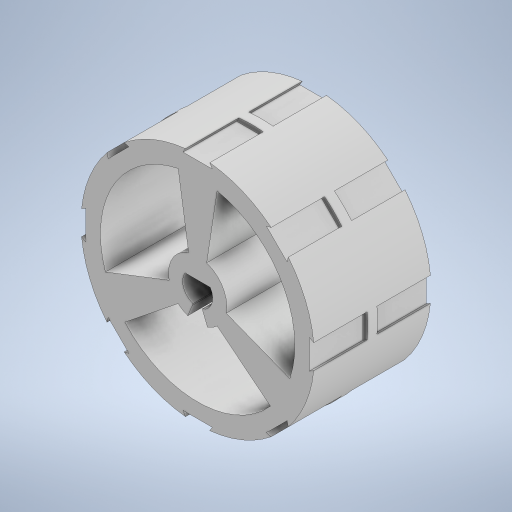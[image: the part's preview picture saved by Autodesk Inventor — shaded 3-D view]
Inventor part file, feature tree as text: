
AUTODESK INVENTOR PART (.ipt)
format: ipt  version: 2024 (Build 280153000, 153)  size: 365,568 bytes
history: native  units: mm
features: extrude x5, sketch x5, other x3
ambient origin geometry x8: Origin, YZ Plane, XZ Plane, XY Plane, X Axis, Y Axis, Z Axis, Center Point
bodies: Body1 (feature_tree)
feature tree (13):
  other  "Bryła1"
  extrude  "Wyciągnięcie proste1"  Depth=30.0mm TaperAngle=360.0deg
  other  "Pogrubienie1"
  other  "Pogrubienie2"
  extrude  "Wyciągnięcie proste2"  Depth=12.0mm TaperAngle=0.0deg
  extrude  "Wyciągnięcie proste3"  Depth=0.2mm
  extrude  "Wyciągnięcie proste4"  Depth=0.2mm
  extrude  "Wyciągnięcie proste5"  Depth=0.2mm
  sketch  "Szkic1"
  sketch  "Szkic2"
  sketch  "Szkic3"
  sketch  "Szkic4"
  sketch  "Szkic5"
